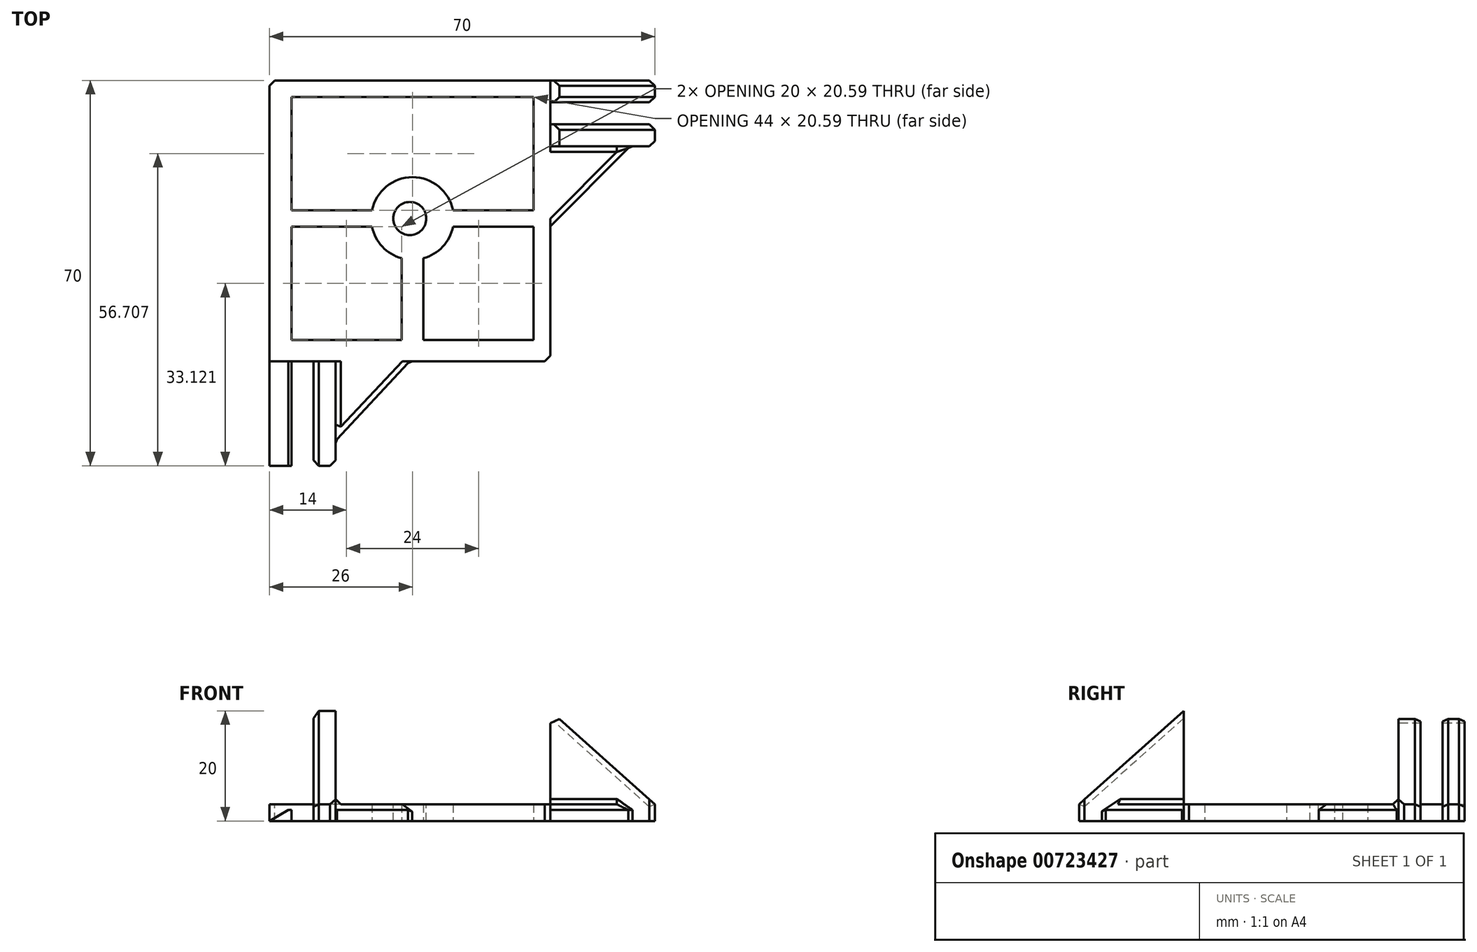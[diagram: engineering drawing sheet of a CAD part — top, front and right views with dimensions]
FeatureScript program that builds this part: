
annotation { "Feature Type Name" : "Feature", "Feature Type Description" : "" }
export const myFeature = defineFeature(function(context is Context, id is Id, definition is map)
    precondition{}
    {
        {
            var Q0;
            Q0=qCreatedBy(makeId("Top.planeOp"),FACE);
            var sketch = newSketch(context, id + "F0", { "sketchPlane" : qUnion([Q0])});
            skLineSegment(sketch, "E0.bottom", {"start": v(0, 0) * mm, "end": v(51, 0) * mm});
            skLineSegment(sketch, "E0.top", {"start": v(0, -51) * mm, "end": v(51, -51) * mm});
            skLineSegment(sketch, "E0.left", {"start": v(0, 0) * mm, "end": v(0, -51) * mm});
            skLineSegment(sketch, "E0.right", {"start": v(51, 0) * mm, "end": v(51, -51) * mm});
            skSolve(sketch);
        }
        {
            var Q0;
            Q0=qSketchRegion(id+"F0",true);
            extrude(context, id + "F1", {"entities" : qUnion([Q0]), "depth" : 3 * mm, "offsetDistance" : 25 * mm});
        }
        {
            var Q0;
            Q0=qCreatedBy(makeId("Top.planeOp"),FACE);
            var sketch = newSketch(context, id + "F2", { "sketchPlane" : qUnion([Q0])});
            skLineSegment(sketch, "E1", {"start": v(0, 0) * mm, "end": v(-19, 0) * mm});
            skLineSegment(sketch, "E2", {"start": v(-19, 0) * mm, "end": v(-19, -4) * mm});
            skLineSegment(sketch, "E3", {"start": v(-19, -4) * mm, "end": v(0, -4) * mm});
            skLineSegment(sketch, "E4", {"start": v(0, -4) * mm, "end": v(0, -8) * mm});
            skLineSegment(sketch, "E5", {"start": v(0, -8) * mm, "end": v(-19, -8) * mm});
            skLineSegment(sketch, "E6", {"start": v(-19, -8) * mm, "end": v(-19, -12) * mm});
            skLineSegment(sketch, "E7", {"start": v(-19, -12) * mm, "end": v(0, -12) * mm});
            skLineSegment(sketch, "E8", {"start": v(0, 0) * mm, "end": v(0, -12) * mm});
            skSolve(sketch);
        }
        {
            var Q0;
            Q0=qSketchRegion(id+"F2",true);
            extrude(context, id + "F3", {"entities" : qUnion([Q0]), "operationType" : NewBodyOperationType.ADD, "depth" : 20 * mm, "offsetDistance" : 25 * mm});
        }
        {
            var Q0;
            Q0=qCreatedBy(makeId("Top.planeOp"),FACE);
            var sketch = newSketch(context, id + "F4", { "sketchPlane" : qUnion([Q0])});
            skLineSegment(sketch, "E9", {"start": v(0, 0) * mm, "end": v(0, -11.5) * mm});
            skLineSegment(sketch, "E10", {"start": v(0, -11.5) * mm, "end": v(-15, -11.5) * mm});
            skLineSegment(sketch, "E11", {"start": v(0, -11.5) * mm, "end": v(0, -26.5) * mm});
            skLineSegment(sketch, "E12", {"start": v(0, -26.5) * mm, "end": v(-15, -11.5) * mm});
            skSolve(sketch);
        }
        {
            var Q0;
            Q0=makeQuery(id+"F4.imprint","IMPRINT",FACE,{"disambiguationData":[TD([[makeQuery(id+"F4.imprint","IMPRINT",EDGE,{"derivedFrom":sQuery(id+"F4.wireOp",EDGE,"E10")}),1.0]])]});
            extrude(context, id + "F5", {"entities" : qUnion([Q0]), "operationType" : NewBodyOperationType.ADD, "depth" : 3 * mm, "offsetDistance" : 25 * mm});
        }
        {
            var Q0;
            Q0=qCreatedBy(makeId("Top.planeOp"),FACE);
            var sketch = newSketch(context, id + "F6", { "sketchPlane" : qUnion([Q0])});
            skLineSegment(sketch, "E13", {"start": v(0, 0) * mm, "end": v(0, -51) * mm});
            skLineSegment(sketch, "E14", {"start": v(0, -51) * mm, "end": v(51, -51) * mm});
            skLineSegment(sketch, "E15", {"start": v(51, -51) * mm, "end": v(51, -70) * mm});
            skLineSegment(sketch, "E16", {"start": v(51, -70) * mm, "end": v(47, -70) * mm});
            skLineSegment(sketch, "E17", {"start": v(47, -70) * mm, "end": v(47, -51) * mm});
            skLineSegment(sketch, "E18", {"start": v(47, -51) * mm, "end": v(43, -51) * mm});
            skLineSegment(sketch, "E19", {"start": v(43, -51) * mm, "end": v(43, -70) * mm});
            skLineSegment(sketch, "E20", {"start": v(43, -70) * mm, "end": v(39, -70) * mm});
            skLineSegment(sketch, "E21", {"start": v(39, -70) * mm, "end": v(39, -51) * mm});
            skLineSegment(sketch, "E22", {"start": v(39, -51) * mm, "end": v(51, -51) * mm});
            skSolve(sketch);
        }
        {
            var Q0;
            Q0=qCreatedBy(makeId("Top.planeOp"),FACE);
            var sketch = newSketch(context, id + "F7", { "sketchPlane" : qUnion([Q0])});
            skLineSegment(sketch, "E23", {"start": v(0, 0) * mm, "end": v(0, -51) * mm});
            skLineSegment(sketch, "E24", {"start": v(0, -51) * mm, "end": v(51, -51) * mm});
            skLineSegment(sketch, "E25", {"start": v(51, -51) * mm, "end": v(39.5, -51) * mm});
            skLineSegment(sketch, "E26", {"start": v(39.5, -51) * mm, "end": v(39.5, -66) * mm});
            skLineSegment(sketch, "E27", {"start": v(39.5, -66) * mm, "end": v(25.5, -51) * mm});
            skLineSegment(sketch, "E28", {"start": v(25.5, -51) * mm, "end": v(39.5, -51) * mm});
            skSolve(sketch);
        }
        {
            var Q0;
            Q0=qSketchRegion(id+"F7",true);
            extrude(context, id + "F8", {"entities" : qUnion([Q0]), "operationType" : NewBodyOperationType.ADD, "depth" : 3 * mm, "offsetDistance" : 25 * mm});
        }
        {
            var Q0;
            Q0=makeQuery(id+"F8.opExtrude","CAP_EDGE",EDGE,{"disambiguationData":[OSD([sQuery(id+"F7.wireOp",EDGE,"E27")])],"isStart":false});
            chamfer(context, id + "F9", {"entities" : qUnion([Q0]), "width" : 1 * mm, "tangentPropagation" : true});
        }
        {
            var Q0;
            Q0=makeQuery(id+"F8.boolean.opBoolean","MERGE",FACE,{"derivedFrom":[makeQuery(id+"F5.boolean.opBoolean","MERGE",FACE,{"derivedFrom":[makeQuery(id+"F1.opExtrude","CAP_FACE",FACE,{"disambiguationData":[OSD([sQuery(id+"F0.wireOp",EDGE,"E0.bottom"),sQuery(id+"F0.wireOp",EDGE,"E0.top"),sQuery(id+"F0.wireOp",EDGE,"E0.left"),sQuery(id+"F0.wireOp",EDGE,"E0.right")])],"isStart":false}),makeQuery(id+"F5.opExtrude","CAP_FACE",FACE,{"disambiguationData":[OSD([sQuery(id+"F4.wireOp",EDGE,"E10"),sQuery(id+"F4.wireOp",EDGE,"E11"),sQuery(id+"F4.wireOp",EDGE,"E12")])],"isStart":false})]}),makeQuery(id+"F8.opExtrude","CAP_FACE",FACE,{"disambiguationData":[OSD([sQuery(id+"F7.wireOp",EDGE,"E26"),sQuery(id+"F7.wireOp",EDGE,"E27"),sQuery(id+"F7.wireOp",EDGE,"E28")])],"isStart":false})]});
            var sketch = newSketch(context, id + "F10", { "sketchPlane" : qUnion([Q0])});
            skCircle(sketch, "E29", {"center": v(25.5, -25.09) * mm, "radius": 3 * mm});
            skPoint(sketch, "E29.centerSnap0", {"position": v(25.5, 0) * mm});
            skSolve(sketch);
        }
        {
            var Q0;
            Q0=qSketchRegion(id+"F10",true);
            extrude(context, id + "F11", {"entities" : qUnion([Q0]), "operationType" : NewBodyOperationType.REMOVE, "oppositeDirection" : true, "depth" : 25 * mm, "offsetDistance" : 25 * mm});
        }
        {
            var Q0;
            {var subQ0=sQuery(id+"F6.wireOp",EDGE,"E19");Q0=makeQuery(id+"F6.imprint","IMPRINT",FACE,{"disambiguationData":[TD([[makeQuery(id+"F6.imprint","IMPRINT",EDGE,{"derivedFrom":subQ0}),-1.0]])]});}
            extrude(context, id + "F12", {"entities" : qUnion([Q0]), "operationType" : NewBodyOperationType.ADD, "depth" : 20 * mm, "offsetDistance" : 25 * mm});
        }
        {
            var Q0;
            Q0=qSketchRegion(id+"F6",true);
            extrude(context, id + "F13", {"entities" : qUnion([Q0]), "operationType" : NewBodyOperationType.ADD, "depth" : 2 * mm, "offsetDistance" : 25 * mm});
        }
        {
            var Q0;
            Q0=makeQuery(id+"F13.opExtrude","CAP_EDGE",EDGE,{"disambiguationData":[OSD([sQuery(id+"F6.wireOp",EDGE,"E15")])],"isStart":false});
            chamfer(context, id + "F14", {"entities" : qUnion([Q0]), "chamferType" : ChamferType.OFFSET_ANGLE, "width" : 2 * mm, "oppositeDirection" : false, "angle" : 60 * degree});
        }
        {
            var Q0;
            Q0=qCreatedBy(makeId("Top.planeOp"),FACE);
            var sketch = newSketch(context, id + "F15", { "sketchPlane" : qUnion([Q0])});
            skCircle(sketch, "E30", {"center": v(25, -25.09) * mm, "radius": 7.5 * mm});
            skLineSegment(sketch, "E31", {"start": v(0, 0) * mm, "end": v(0, -3) * mm});
            skLineSegment(sketch, "E32", {"start": v(0, -3) * mm, "end": v(25, -3) * mm});
            skLineSegment(sketch, "E33", {"start": v(25, -3) * mm, "end": v(23, -3) * mm});
            skLineSegment(sketch, "E34", {"start": v(23, -3) * mm, "end": v(23, -17.86) * mm});
            skLineSegment(sketch, "E35", {"start": v(0, -3) * mm, "end": v(3, -3) * mm});
            skLineSegment(sketch, "E36", {"start": v(3, -3) * mm, "end": v(3, -25.09) * mm});
            skLineSegment(sketch, "E37", {"start": v(3, -25.09) * mm, "end": v(3, -23.59) * mm});
            skLineSegment(sketch, "E38", {"start": v(3, -23.59) * mm, "end": v(17.65, -23.59) * mm});
            skLineSegment(sketch, "E39", {"start": v(25, -25.09) * mm, "end": v(51, -25.09) * mm});
            skLineSegment(sketch, "E40", {"start": v(25, -25.09) * mm, "end": v(25, -51) * mm});
            skLineSegment(sketch, "E41.MirrorCS", {"start": v(3, -26.59) * mm, "end": v(17.65, -26.59) * mm});
            skLineSegment(sketch, "E42.MirrorCS", {"start": v(3, -47.17) * mm, "end": v(3, -25.09) * mm});
            skLineSegment(sketch, "E43.MirrorCS", {"start": v(0, -47.17) * mm, "end": v(25, -47.17) * mm});
            skLineSegment(sketch, "E44.MirrorCS", {"start": v(23, -47.17) * mm, "end": v(23, -32.31) * mm});
            skLineSegment(sketch, "E45.MirrorCS", {"start": v(27, -47.17) * mm, "end": v(27, -32.31) * mm});
            skLineSegment(sketch, "E46.MirrorCS", {"start": v(50, -47.17) * mm, "end": v(25, -47.17) * mm});
            skLineSegment(sketch, "E47.MirrorCS", {"start": v(47, -47.17) * mm, "end": v(47, -25.09) * mm});
            skLineSegment(sketch, "E48.MirrorCS", {"start": v(47, -26.59) * mm, "end": v(32.35, -26.59) * mm});
            skLineSegment(sketch, "E49.MirrorCS", {"start": v(47, -23.59) * mm, "end": v(32.35, -23.59) * mm});
            skLineSegment(sketch, "E50.MirrorCS", {"start": v(47, -3) * mm, "end": v(47, -25.09) * mm});
            skLineSegment(sketch, "E51.MirrorCS", {"start": v(50, -3) * mm, "end": v(25, -3) * mm});
            skLineSegment(sketch, "E52.MirrorCS", {"start": v(27, -3) * mm, "end": v(27, -17.86) * mm});
            skLineSegment(sketch, "E53", {"start": v(0, 0) * mm, "end": v(0, -47.17) * mm});
            skSolve(sketch);
        }
        {
            var Q0;
            {var subQ4=sQuery(id+"F15.wireOp",EDGE,"E49.MirrorCS");Q0=makeQuery(id+"F15.imprint","IMPRINT",FACE,{"disambiguationData":[TD([[makeQuery(id+"F15.imprint","IMPRINT",EDGE,{"derivedFrom":subQ4}),-1.0]])]});}
            var Q1;
            {var subQ4=sQuery(id+"F15.wireOp",EDGE,"E45.MirrorCS");Q1=makeQuery(id+"F15.imprint","IMPRINT",FACE,{"disambiguationData":[TD([[makeQuery(id+"F15.imprint","IMPRINT",EDGE,{"derivedFrom":subQ4}),-1.0]])]});}
            var Q2;
            {var subQ1=sQuery(id+"F15.wireOp",EDGE,"E41.MirrorCS");Q2=makeQuery(id+"F15.imprint","IMPRINT",FACE,{"disambiguationData":[TD([[makeQuery(id+"F15.imprint","IMPRINT",EDGE,{"derivedFrom":subQ1}),-1.0]])]});}
            var Q3;
            Q3=makeQuery(id+"F15.imprint","IMPRINT",FACE,{"disambiguationData":[TD([[makeQuery(id+"F15.imprint","IMPRINT",EDGE,{"derivedFrom":sQuery(id+"F15.wireOp",EDGE,"E32")}),-1.0]])]});
            extrude(context, id + "F16", {"entities" : qUnion([Q0, Q1, Q2, Q3]), "operationType" : NewBodyOperationType.REMOVE, "depth" : 25 * mm, "offsetDistance" : 25 * mm});
        }
        {
            var Q0;
            Q0=makeQuery(id+"F3.opExtrude","SWEPT_FACE",FACE,{"disambiguationData":[OSD([sQuery(id+"F2.wireOp",EDGE,"E7")])]});
            var sketch = newSketch(context, id + "F17", { "sketchPlane" : qUnion([Q0])});
            skLineSegment(sketch, "E54", {"start": v(-19, 20) * mm, "end": v(-19, 3) * mm});
            skLineSegment(sketch, "E55", {"start": v(-19, 3) * mm, "end": v(0, 3) * mm});
            skLineSegment(sketch, "E56", {"start": v(-19, 20) * mm, "end": v(0, 20) * mm});
            skLineSegment(sketch, "E57", {"start": v(0, 20) * mm, "end": v(-19, 3) * mm});
            skSolve(sketch);
        }
        {
            var Q0;
            Q0=qSketchRegion(id+"F17",true);
            extrude(context, id + "F18", {"entities" : qUnion([Q0]), "operationType" : NewBodyOperationType.REMOVE, "oppositeDirection" : true, "depth" : 25 * mm, "offsetDistance" : 25 * mm});
        }
        {
            var Q0;
            Q0=makeQuery(id+"F12.opExtrude","SWEPT_FACE",FACE,{"disambiguationData":[OSD([sQuery(id+"F6.wireOp",EDGE,"E21")])]});
            var sketch = newSketch(context, id + "F19", { "sketchPlane" : qUnion([Q0])});
            skLineSegment(sketch, "E58", {"start": v(51, 3) * mm, "end": v(70, 3) * mm});
            skLineSegment(sketch, "E59", {"start": v(70, 3) * mm, "end": v(51, 20) * mm});
            skLineSegment(sketch, "E60", {"start": v(51, 20) * mm, "end": v(70, 20) * mm});
            skLineSegment(sketch, "E61", {"start": v(70, 20) * mm, "end": v(70, 3) * mm});
            skSolve(sketch);
        }
        {
            var Q0;
            Q0=qSketchRegion(id+"F19",true);
            extrude(context, id + "F20", {"entities" : qUnion([Q0]), "operationType" : NewBodyOperationType.REMOVE, "oppositeDirection" : true, "depth" : 25 * mm, "offsetDistance" : 25 * mm});
        }
        {
            var Q0;
            Q0=makeQuery(id+"F18.boolean.opBoolean","INTERSECT",EDGE,{"derivedFrom":[makeQuery(id+"F3.boolean.opBoolean","MERGE",FACE,{"derivedFrom":[makeQuery(id+"F1.opExtrude","SWEPT_FACE",FACE,{"disambiguationData":[OSD([sQuery(id+"F0.wireOp",EDGE,"E0.bottom")])]}),makeQuery(id+"F3.opExtrude","SWEPT_FACE",FACE,{"disambiguationData":[OSD([sQuery(id+"F2.wireOp",EDGE,"E1")])]})]}),makeQuery(id+"F18.opExtrude","SWEPT_FACE",FACE,{"disambiguationData":[OSD([sQuery(id+"F17.wireOp",EDGE,"E57")])]})]});
            var Q1;
            Q1=makeQuery(id+"F18.boolean.opBoolean","INTERSECT",EDGE,{"derivedFrom":[makeQuery(id+"F3.opExtrude","SWEPT_FACE",FACE,{"disambiguationData":[OSD([sQuery(id+"F2.wireOp",EDGE,"E3")])]}),makeQuery(id+"F18.opExtrude","SWEPT_FACE",FACE,{"disambiguationData":[OSD([sQuery(id+"F17.wireOp",EDGE,"E57")])]})]});
            var Q2;
            Q2=makeQuery(id+"F18.boolean.opBoolean","INTERSECT",EDGE,{"derivedFrom":[makeQuery(id+"F3.opExtrude","SWEPT_FACE",FACE,{"disambiguationData":[OSD([sQuery(id+"F2.wireOp",EDGE,"E5")])]}),makeQuery(id+"F18.opExtrude","SWEPT_FACE",FACE,{"disambiguationData":[OSD([sQuery(id+"F17.wireOp",EDGE,"E57")])]})]});
            var Q3;
            Q3=makeQuery(id+"F18.boolean.opBoolean","COPY",EDGE,{"derivedFrom":makeQuery(id+"F18.opExtrude","CAP_EDGE",EDGE,{"disambiguationData":[OSD([sQuery(id+"F17.wireOp",EDGE,"E57")])],"isStart":true})});
            var Q4;
            Q4=makeQuery(id+"F5.opExtrude","CAP_EDGE",EDGE,{"disambiguationData":[OSD([sQuery(id+"F4.wireOp",EDGE,"E12")])],"isStart":false});
            var Q5;
            Q5=makeQuery(id+"F20.boolean.opBoolean","COPY",EDGE,{"derivedFrom":makeQuery(id+"F20.opExtrude","CAP_EDGE",EDGE,{"disambiguationData":[OSD([sQuery(id+"F19.wireOp",EDGE,"E59")])],"isStart":true})});
            var Q6;
            Q6=makeQuery(id+"F20.boolean.opBoolean","INTERSECT",EDGE,{"derivedFrom":[makeQuery(id+"F12.opExtrude","SWEPT_FACE",FACE,{"disambiguationData":[OSD([sQuery(id+"F6.wireOp",EDGE,"E19")])]}),makeQuery(id+"F20.opExtrude","SWEPT_FACE",FACE,{"disambiguationData":[OSD([sQuery(id+"F19.wireOp",EDGE,"E59")])]})]});
            var Q7;
            {var subQ0=sQuery(id+"F2.wireOp",EDGE,"E8");Q7=makeQuery(id+"F18.boolean.opBoolean","MERGE",EDGE,{"derivedFrom":[makeQuery(id+"F3.opExtrude","CAP_EDGE",EDGE,{"disambiguationData":[OSD([subQ0]),TDD([makeQuery(id+"F2.imprint","IMPRINT",EDGE,{"disambiguationData":[TD([[makeQuery(id+"F2.imprint","INTERSECT",VERTEX,{"derivedFrom":[sQuery(id+"F2.wireOp",EDGE,"E1"),subQ0]}),-1.0]])],"derivedFrom":subQ0})])],"isStart":false}),makeQuery(id+"F18.opExtrude","SWEPT_EDGE",EDGE,{"disambiguationData":[OSD([sQuery(id+"F2.wireOp",EDGE,"E7"),subQ0,sQuery(id+"F17.wireOp",EDGE,"E56"),sQuery(id+"F17.wireOp",EDGE,"E57")])]})]});}
            var Q8;
            {var subQ0=sQuery(id+"F2.wireOp",EDGE,"E8");var subQ1=sQuery(id+"F2.wireOp",EDGE,"E7");Q8=makeQuery(id+"F18.boolean.opBoolean","MERGE",EDGE,{"derivedFrom":[makeQuery(id+"F3.opExtrude","CAP_EDGE",EDGE,{"disambiguationData":[OSD([subQ0]),TDD([makeQuery(id+"F2.imprint","IMPRINT",EDGE,{"disambiguationData":[TD([[makeQuery(id+"F2.imprint","INTERSECT",VERTEX,{"derivedFrom":[sQuery(id+"F2.wireOp",EDGE,"E5"),subQ0]}),-1.0]])],"derivedFrom":subQ0})])],"isStart":false}),makeQuery(id+"F18.opExtrude","SWEPT_EDGE",EDGE,{"disambiguationData":[OSD([subQ1,subQ0,sQuery(id+"F17.wireOp",EDGE,"E56"),sQuery(id+"F17.wireOp",EDGE,"E57")])]})]});}
            var Q9;
            {var subQ0=sQuery(id+"F6.wireOp",EDGE,"E22");Q9=makeQuery(id+"F20.boolean.opBoolean","MERGE",EDGE,{"derivedFrom":[makeQuery(id+"F12.opExtrude","CAP_EDGE",EDGE,{"disambiguationData":[OSD([subQ0])],"isStart":false}),makeQuery(id+"F20.opExtrude","SWEPT_EDGE",EDGE,{"disambiguationData":[OSD([sQuery(id+"F6.wireOp",EDGE,"E21"),subQ0,sQuery(id+"F19.wireOp",EDGE,"E59"),sQuery(id+"F19.wireOp",EDGE,"E60")])]})]});}
            var Q10;
            {var subQ0=sQuery(id+"F17.wireOp",EDGE,"E57");Q10=makeQuery(id+"F18.boolean.opBoolean","COPY",EDGE,{"disambiguationData":[topologyDisambiguationEdgeConnected([makeQuery(id+"F3.opExtrude","SWEPT_FACE",FACE,{"disambiguationData":[OSD([sQuery(id+"F2.wireOp",EDGE,"E2")])]})])],"derivedFrom":makeQuery(id+"F18.opExtrude","SWEPT_EDGE",EDGE,{"disambiguationData":[OSD([sQuery(id+"F2.wireOp",EDGE,"E6"),sQuery(id+"F2.wireOp",EDGE,"E7"),sQuery(id+"F17.wireOp",EDGE,"E54"),sQuery(id+"F17.wireOp",EDGE,"E55"),subQ0])]})});}
            var Q11;
            {var subQ0=sQuery(id+"F2.wireOp",EDGE,"E6");var subQ1=sQuery(id+"F17.wireOp",EDGE,"E57");Q11=makeQuery(id+"F18.boolean.opBoolean","COPY",EDGE,{"disambiguationData":[topologyDisambiguationEdgeConnected([makeQuery(id+"F3.opExtrude","SWEPT_FACE",FACE,{"disambiguationData":[OSD([subQ0])]})])],"derivedFrom":makeQuery(id+"F18.opExtrude","SWEPT_EDGE",EDGE,{"disambiguationData":[OSD([subQ0,sQuery(id+"F2.wireOp",EDGE,"E7"),sQuery(id+"F17.wireOp",EDGE,"E54"),sQuery(id+"F17.wireOp",EDGE,"E55"),subQ1])]})});}
            var Q12;
            Q12=makeQuery(id+"F20.boolean.opBoolean","COPY",EDGE,{"derivedFrom":makeQuery(id+"F20.opExtrude","SWEPT_EDGE",EDGE,{"disambiguationData":[OSD([sQuery(id+"F6.wireOp",EDGE,"E20"),sQuery(id+"F6.wireOp",EDGE,"E21"),sQuery(id+"F19.wireOp",EDGE,"E58"),sQuery(id+"F19.wireOp",EDGE,"E59"),sQuery(id+"F19.wireOp",EDGE,"E61")])]})});
            var Q13;
            Q13=makeQuery(id+"F5.boolean.opBoolean","INTERSECT",EDGE,{"derivedFrom":[makeQuery(id+"F3.opExtrude","SWEPT_FACE",FACE,{"disambiguationData":[OSD([sQuery(id+"F2.wireOp",EDGE,"E7")])]}),makeQuery(id+"F5.opExtrude","CAP_FACE",FACE,{"disambiguationData":[OSD([sQuery(id+"F4.wireOp",EDGE,"E10"),sQuery(id+"F4.wireOp",EDGE,"E11"),sQuery(id+"F4.wireOp",EDGE,"E12")])],"isStart":false})]});
            var Q14;
            Q14=makeQuery(id+"F12.boolean.opBoolean","INTERSECT",EDGE,{"derivedFrom":[makeQuery(id+"F8.boolean.opBoolean","MERGE",FACE,{"derivedFrom":[makeQuery(id+"F5.boolean.opBoolean","MERGE",FACE,{"derivedFrom":[makeQuery(id+"F1.opExtrude","CAP_FACE",FACE,{"disambiguationData":[OSD([sQuery(id+"F0.wireOp",EDGE,"E0.bottom"),sQuery(id+"F0.wireOp",EDGE,"E0.top"),sQuery(id+"F0.wireOp",EDGE,"E0.left"),sQuery(id+"F0.wireOp",EDGE,"E0.right")])],"isStart":false}),makeQuery(id+"F5.opExtrude","CAP_FACE",FACE,{"disambiguationData":[OSD([sQuery(id+"F4.wireOp",EDGE,"E10"),sQuery(id+"F4.wireOp",EDGE,"E11"),sQuery(id+"F4.wireOp",EDGE,"E12")])],"isStart":false})]}),makeQuery(id+"F8.opExtrude","CAP_FACE",FACE,{"disambiguationData":[OSD([sQuery(id+"F7.wireOp",EDGE,"E26"),sQuery(id+"F7.wireOp",EDGE,"E27"),sQuery(id+"F7.wireOp",EDGE,"E28")])],"isStart":false})]}),makeQuery(id+"F12.opExtrude","SWEPT_FACE",FACE,{"disambiguationData":[OSD([sQuery(id+"F6.wireOp",EDGE,"E21")])]})]});
            chamfer(context, id + "F21", {"entities" : qUnion([Q0, Q1, Q2, Q3, Q4, Q5, Q6, Q7, Q8, Q9, Q10, Q11, Q12, Q13, Q14]), "width" : 1 * mm, "tangentPropagation" : true});
        }
        {
            var Q0;
            Q0=makeQuery(id+"F1.opExtrude","SWEPT_BODY",BODY,{"disambiguationData":[OSD([sQuery(id+"F0.wireOp",EDGE,"E0.bottom"),sQuery(id+"F0.wireOp",EDGE,"E0.top"),sQuery(id+"F0.wireOp",EDGE,"E0.left"),sQuery(id+"F0.wireOp",EDGE,"E0.right")])]});
            var Q1;
            Q1=qCreatedBy(makeId("Right.planeOp"),FACE);
            mirror(context, id + "F22", {"entities" : qUnion([Q0]), "mirrorPlane" : qUnion([Q1])});
        }
        {
            var Q0;
            Q0=makeQuery(id+"F1.opExtrude","SWEPT_BODY",BODY,{"disambiguationData":[OSD([sQuery(id+"F0.wireOp",EDGE,"E0.bottom"),sQuery(id+"F0.wireOp",EDGE,"E0.top"),sQuery(id+"F0.wireOp",EDGE,"E0.left"),sQuery(id+"F0.wireOp",EDGE,"E0.right")])]});
            deleteBodies(context, id + "F23", {"entities" : qUnion([Q0])});
        }
        {
            var Q0;
            Q0=makeQuery(id+"F22.opPattern","COPY",EDGE,{"derivedFrom":makeQuery(id+"F1.opExtrude","SWEPT_EDGE",EDGE,{"disambiguationData":[OSD([sQuery(id+"F0.wireOp",EDGE,"E0.top"),sQuery(id+"F0.wireOp",EDGE,"E0.left")])]}),"instanceName":"1"});
            var Q1;
            Q1=makeQuery(id+"F22.opPattern","COPY",EDGE,{"derivedFrom":makeQuery(id+"F5.opExtrude","SWEPT_EDGE",EDGE,{"disambiguationData":[OSD([sQuery(id+"F4.wireOp",EDGE,"E11"),sQuery(id+"F4.wireOp",EDGE,"E12")])]}),"instanceName":"1"});
            var Q2;
            Q2=makeQuery(id+"F22.opPattern","COPY",EDGE,{"derivedFrom":makeQuery(id+"F3.opExtrude","SWEPT_EDGE",EDGE,{"disambiguationData":[OSD([sQuery(id+"F2.wireOp",EDGE,"E6"),sQuery(id+"F2.wireOp",EDGE,"E7")])]}),"instanceName":"1"});
            var Q3;
            Q3=makeQuery(id+"F22.opPattern","COPY",EDGE,{"derivedFrom":makeQuery(id+"F3.opExtrude","SWEPT_EDGE",EDGE,{"disambiguationData":[OSD([sQuery(id+"F2.wireOp",EDGE,"E5"),sQuery(id+"F2.wireOp",EDGE,"E6")])]}),"instanceName":"1"});
            var Q4;
            Q4=makeQuery(id+"F22.opPattern","COPY",EDGE,{"derivedFrom":makeQuery(id+"F3.opExtrude","SWEPT_EDGE",EDGE,{"disambiguationData":[OSD([sQuery(id+"F2.wireOp",EDGE,"E2"),sQuery(id+"F2.wireOp",EDGE,"E3")])]}),"instanceName":"1"});
            var Q5;
            Q5=makeQuery(id+"F22.opPattern","COPY",EDGE,{"derivedFrom":makeQuery(id+"F3.opExtrude","SWEPT_EDGE",EDGE,{"disambiguationData":[OSD([sQuery(id+"F2.wireOp",EDGE,"E1"),sQuery(id+"F2.wireOp",EDGE,"E2")])]}),"instanceName":"1"});
            var Q6;
            Q6=makeQuery(id+"F22.opPattern","COPY",EDGE,{"derivedFrom":makeQuery(id+"F12.opExtrude","SWEPT_EDGE",EDGE,{"disambiguationData":[OSD([sQuery(id+"F6.wireOp",EDGE,"E19"),sQuery(id+"F6.wireOp",EDGE,"E20")])]}),"instanceName":"1"});
            var Q7;
            Q7=makeQuery(id+"F22.opPattern","COPY",EDGE,{"derivedFrom":makeQuery(id+"F12.opExtrude","SWEPT_EDGE",EDGE,{"disambiguationData":[OSD([sQuery(id+"F6.wireOp",EDGE,"E20"),sQuery(id+"F6.wireOp",EDGE,"E21")])]}),"instanceName":"1"});
            var Q8;
            Q8=makeQuery(id+"F22.opPattern","COPY",EDGE,{"derivedFrom":makeQuery(id+"F12.boolean.opBoolean","INTERSECT",EDGE,{"derivedFrom":[makeQuery(id+"F8.opExtrude","SWEPT_FACE",FACE,{"disambiguationData":[OSD([sQuery(id+"F7.wireOp",EDGE,"E27")])]}),makeQuery(id+"F12.opExtrude","SWEPT_FACE",FACE,{"disambiguationData":[OSD([sQuery(id+"F6.wireOp",EDGE,"E21")])]})]}),"instanceName":"1"});
            var Q9;
            Q9=makeQuery(id+"F22.opPattern","COPY",EDGE,{"derivedFrom":makeQuery(id+"F8.opExtrude","SWEPT_EDGE",EDGE,{"disambiguationData":[OSD([sQuery(id+"F7.wireOp",EDGE,"E27"),sQuery(id+"F7.wireOp",EDGE,"E28")])]}),"instanceName":"1"});
            var Q10;
            Q10=makeQuery(id+"F22.opPattern","COPY",EDGE,{"derivedFrom":makeQuery(id+"F1.opExtrude","SWEPT_EDGE",EDGE,{"disambiguationData":[OSD([sQuery(id+"F0.wireOp",EDGE,"E0.bottom"),sQuery(id+"F0.wireOp",EDGE,"E0.right")])]}),"instanceName":"1"});
            chamfer(context, id + "F24", {"entities" : qUnion([Q0, Q1, Q2, Q3, Q4, Q5, Q6, Q7, Q8, Q9, Q10]), "width" : 1 * mm, "tangentPropagation" : true});
        }
    });
